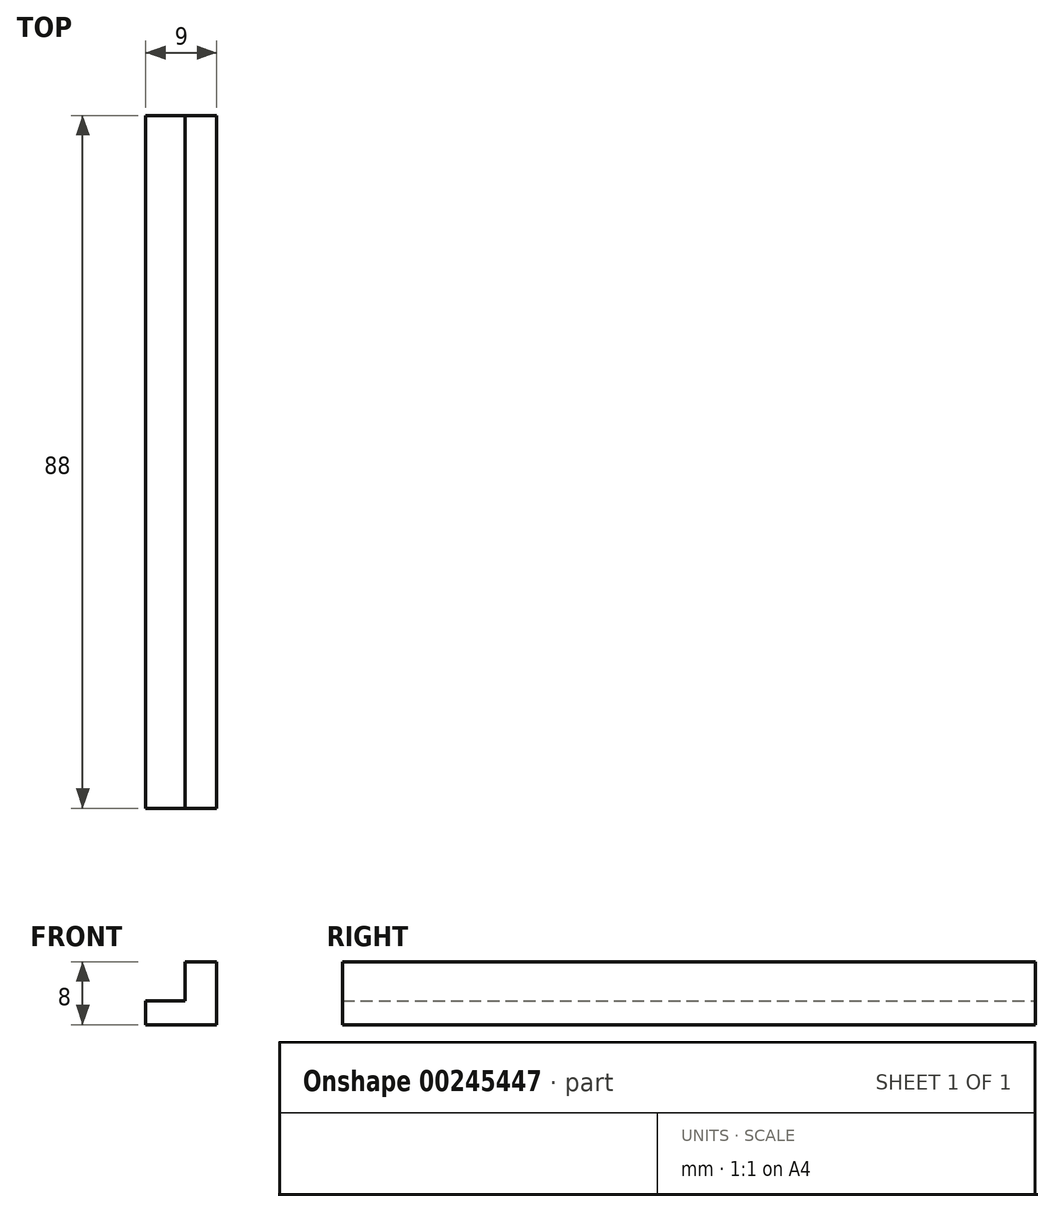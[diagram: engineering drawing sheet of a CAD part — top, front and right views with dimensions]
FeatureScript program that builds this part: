
annotation { "Feature Type Name" : "Feature", "Feature Type Description" : "" }
export const myFeature = defineFeature(function(context is Context, id is Id, definition is map)
    precondition{}
    {
        {
            var Q0;
            Q0=qCreatedBy(makeId("Front.planeOp"),FACE);
            var sketch = newSketch(context, id + "F0", { "sketchPlane" : qUnion([Q0])});
            skLineSegment(sketch, "E0", {"start": v(0, 0) * mm, "end": v(0, 3) * mm});
            skLineSegment(sketch, "E1", {"start": v(0, 3) * mm, "end": v(5, 3) * mm});
            skLineSegment(sketch, "E2", {"start": v(5, 3) * mm, "end": v(5, 8) * mm});
            skLineSegment(sketch, "E3", {"start": v(5, 8) * mm, "end": v(9, 8) * mm});
            skLineSegment(sketch, "E4", {"start": v(9, 8) * mm, "end": v(9, 0) * mm});
            skLineSegment(sketch, "E5", {"start": v(9, 0) * mm, "end": v(0, 0) * mm});
            skSolve(sketch);
        }
        {
            var Q0;
            Q0 = qSketchRegion(id + "F0", true);
            extrude(context, id + "F1", {"entities" : qUnion([Q0]), "depth" : 88 * mm});
        }
    });
